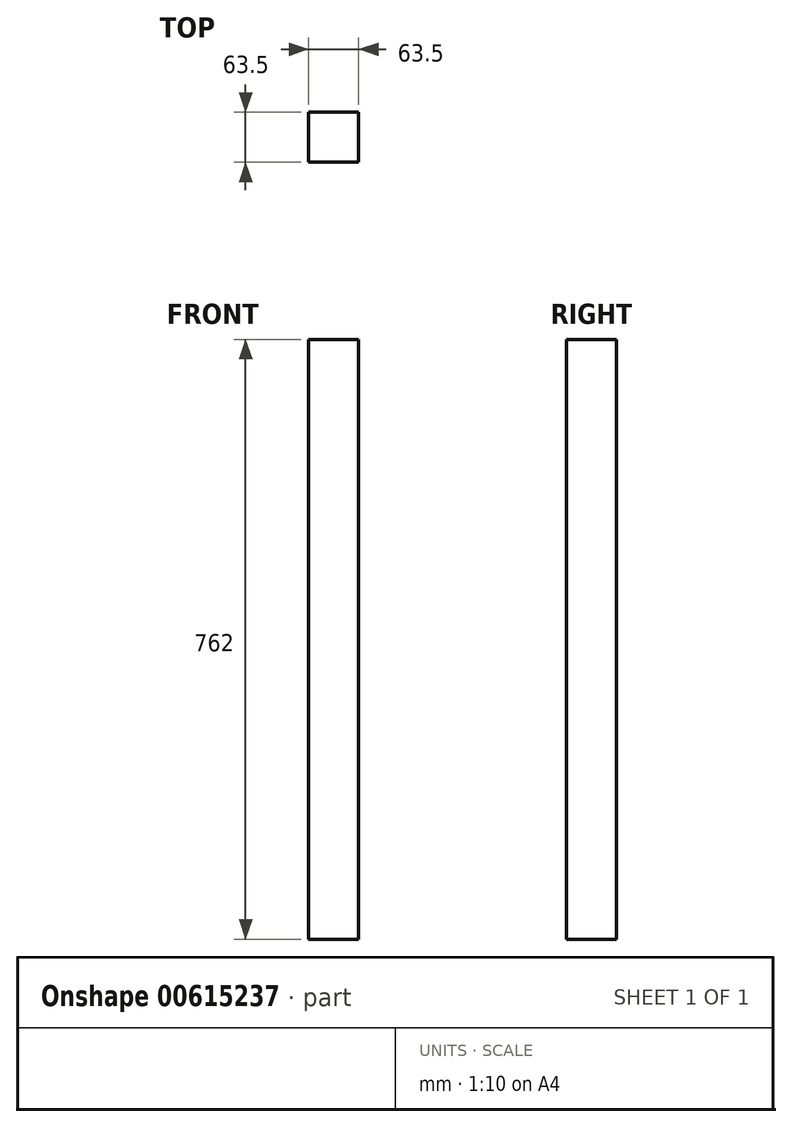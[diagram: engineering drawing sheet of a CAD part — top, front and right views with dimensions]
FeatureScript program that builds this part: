
annotation { "Feature Type Name" : "Feature", "Feature Type Description" : "" }
export const myFeature = defineFeature(function(context is Context, id is Id, definition is map)
    precondition{}
    {
        {
            var Q0;
            Q0=qCreatedBy(makeId("Top.planeOp"),FACE);
            var sketch = newSketch(context, id + "F0", { "sketchPlane" : qUnion([Q0])});
            skLineSegment(sketch, "E0.bottom", {"start": v(0, 0) * mm, "end": v(63.5, 0) * mm});
            skLineSegment(sketch, "E0.top", {"start": v(0, 63.5) * mm, "end": v(63.5, 63.5) * mm});
            skLineSegment(sketch, "E0.left", {"start": v(0, 0) * mm, "end": v(0, 63.5) * mm});
            skLineSegment(sketch, "E0.right", {"start": v(63.5, 0) * mm, "end": v(63.5, 63.5) * mm});
            skSolve(sketch);
        }
        {
            var Q0;
            Q0=makeQuery(id+"F0.imprint","IMPRINT",FACE,{"disambiguationData":[TD([[makeQuery(id+"F0.imprint","IMPRINT",EDGE,{"derivedFrom":sQuery(id+"F0.wireOp",EDGE,"E0.bottom")}),1.0]])]});
            extrude(context, id + "F1", {"entities" : qUnion([Q0]), "depth" : 762 * mm, "offsetDistance" : 25.4 * mm});
        }
    });
